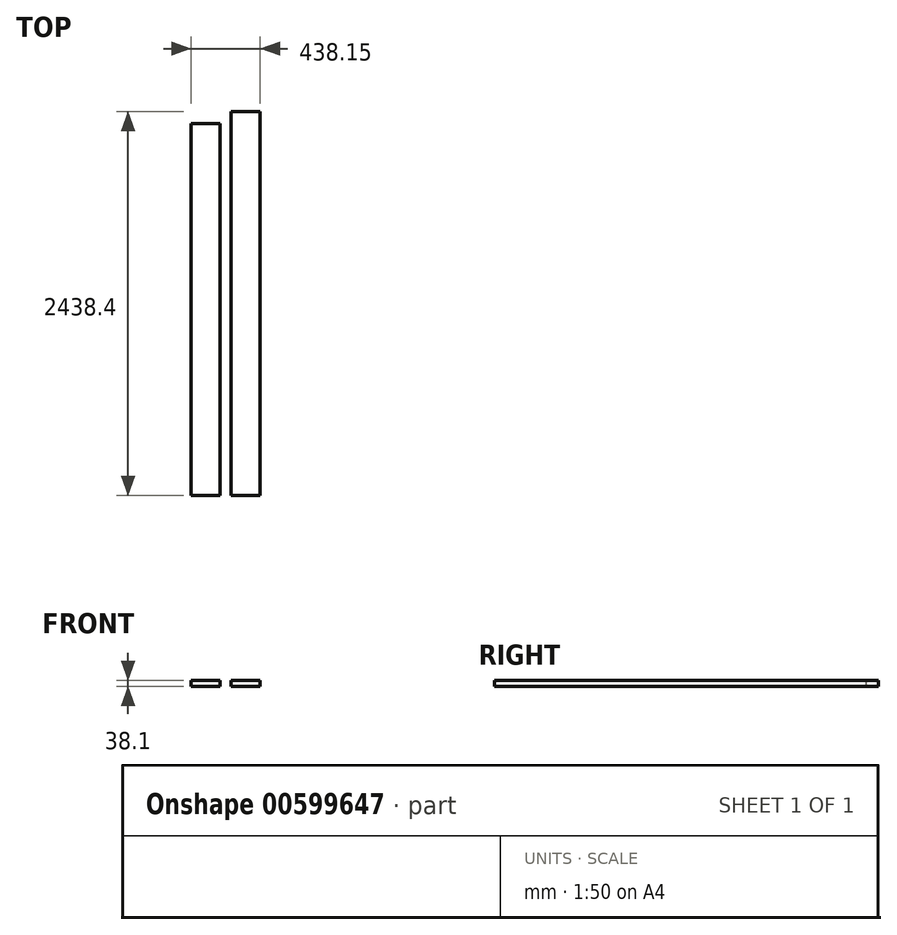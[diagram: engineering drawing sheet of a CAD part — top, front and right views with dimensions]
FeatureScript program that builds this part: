
annotation { "Feature Type Name" : "Feature", "Feature Type Description" : "" }
export const myFeature = defineFeature(function(context is Context, id is Id, definition is map)
    precondition{}
    {
        {
            var Q0;
            Q0=qCreatedBy(makeId("Front.planeOp"),FACE);
            var sketch = newSketch(context, id + "F0", { "sketchPlane" : qUnion([Q0])});
            skLineSegment(sketch, "E0.bottom", {"start": v(0, 0) * mm, "end": v(-184.15, 0) * mm});
            skLineSegment(sketch, "E0.top", {"start": v(0, 38.1) * mm, "end": v(-184.15, 38.1) * mm});
            skLineSegment(sketch, "E0.left", {"start": v(0, 0) * mm, "end": v(0, 38.1) * mm});
            skLineSegment(sketch, "E0.right", {"start": v(-184.15, 0) * mm, "end": v(-184.15, 38.1) * mm});
            skSolve(sketch);
        }
        {
            var Q0;
            Q0=makeQuery(id+"F0.imprint","IMPRINT",FACE,{"disambiguationData":[TD([[makeQuery(id+"F0.imprint","IMPRINT",EDGE,{"derivedFrom":sQuery(id+"F0.wireOp",EDGE,"E0.bottom")}),-1.0]])]});
            extrude(context, id + "F1", {"entities" : qUnion([Q0]), "depth" : 2362.2 * mm, "offsetDistance" : 25.4 * mm});
        }
        {
            var Q0;
            Q0=makeQuery(id+"F1.opExtrude","SWEPT_BODY",BODY,{"disambiguationData":[OSD([sQuery(id+"F0.wireOp",EDGE,"E0.bottom"),sQuery(id+"F0.wireOp",EDGE,"E0.top"),sQuery(id+"F0.wireOp",EDGE,"E0.left"),sQuery(id+"F0.wireOp",EDGE,"E0.right")])]});
            transform(context, id + "F2", {"entities" : qUnion([Q0]), "transformType" : TransformType.TRANSLATION_3D, "dx" : 254 * mm, "dy" : 0 * mm, "dz" : 0 * mm, "makeCopy" : true});
        }
        {
            var Q0;
            Q0=makeQuery(id+"F2.opPattern","COPY",BODY,{"derivedFrom":makeQuery(id+"F1.opExtrude","SWEPT_BODY",BODY,{"disambiguationData":[OSD([sQuery(id+"F0.wireOp",EDGE,"E0.bottom"),sQuery(id+"F0.wireOp",EDGE,"E0.top"),sQuery(id+"F0.wireOp",EDGE,"E0.left"),sQuery(id+"F0.wireOp",EDGE,"E0.right")])]}),"instanceName":"1"});
            deleteBodies(context, id + "F3", {"entities" : qUnion([Q0])});
        }
        {
            var Q0;
            Q0=makeQuery(id+"F1.opExtrude","SWEPT_BODY",BODY,{"disambiguationData":[OSD([sQuery(id+"F0.wireOp",EDGE,"E0.bottom"),sQuery(id+"F0.wireOp",EDGE,"E0.top"),sQuery(id+"F0.wireOp",EDGE,"E0.left"),sQuery(id+"F0.wireOp",EDGE,"E0.right")])]});
            transform(context, id + "F4", {"entities" : qUnion([Q0]), "transformType" : TransformType.TRANSLATION_3D, "dx" : 254 * mm, "dy" : 0 * mm, "dz" : 0 * mm, "makeCopy" : true});
        }
        {
            var Q0;
            Q0=makeQuery(id+"F4.opPattern","COPY",BODY,{"derivedFrom":makeQuery(id+"F1.opExtrude","SWEPT_BODY",BODY,{"disambiguationData":[OSD([sQuery(id+"F0.wireOp",EDGE,"E0.bottom"),sQuery(id+"F0.wireOp",EDGE,"E0.top"),sQuery(id+"F0.wireOp",EDGE,"E0.left"),sQuery(id+"F0.wireOp",EDGE,"E0.right")])]}),"instanceName":"1"});
            deleteBodies(context, id + "F5", {"entities" : qUnion([Q0])});
        }
        {
            var Q0;
            Q0 = qSketchRegion(id + "F0", true);
            extrude(context, id + "F6", {"entities" : qUnion([Q0]), "oppositeDirection" : true, "depth" : 2438.4 * mm, "offsetDistance" : 25.4 * mm});
        }
        {
            var Q0;
            Q0=makeQuery(id+"F6.opExtrude","SWEPT_BODY",BODY,{"disambiguationData":[OSD([sQuery(id+"F0.wireOp",EDGE,"E0.bottom"),sQuery(id+"F0.wireOp",EDGE,"E0.top"),sQuery(id+"F0.wireOp",EDGE,"E0.left"),sQuery(id+"F0.wireOp",EDGE,"E0.right")])]});
            transform(context, id + "F7", {"entities" : qUnion([Q0]), "transformType" : TransformType.TRANSLATION_3D, "dx" : 254 * mm, "dy" : -2362.2 * mm, "dz" : 0 * mm, "makeCopy" : true});
        }
        {
            var Q0;
            Q0=makeQuery(id+"F6.opExtrude","SWEPT_BODY",BODY,{"disambiguationData":[OSD([sQuery(id+"F0.wireOp",EDGE,"E0.bottom"),sQuery(id+"F0.wireOp",EDGE,"E0.top"),sQuery(id+"F0.wireOp",EDGE,"E0.left"),sQuery(id+"F0.wireOp",EDGE,"E0.right")])]});
            deleteBodies(context, id + "F8", {"entities" : qUnion([Q0])});
        }
    });
